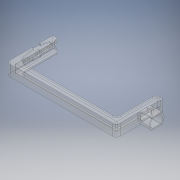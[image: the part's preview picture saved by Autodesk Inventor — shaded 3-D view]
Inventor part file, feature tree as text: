
AUTODESK INVENTOR PART (.ipt)
format: ipt  version: 2018 (Build 220112000, 112)  size: 311,808 bytes
history: native  units: mm
features: extrude x7, sketch x7, fillet x4, chamfer x4
ambient origin geometry x8: Origin, YZ Plane, XZ Plane, XY Plane, X Axis, Y Axis, Z Axis, Center Point
bodies: Solid1 (feature_tree)
feature tree (22):
  extrude  "Phone Profile"  Depth=72.5mm
  extrude  "Front Wall"  Depth=5.0mm
  extrude  "Back Wall"  Depth=155.0mm
  fillet  "Strengthening fillet"  Radius=65.3125mm
  extrude  "Servo Holes"  Depth=11.5mm TaperAngle=0.0deg
  extrude  "Servo indentation"  Depth=5.0mm
  chamfer  "Servo Chamfer 1"  Distance=2.0mm
  chamfer  "Servo Chamfer 2"  Distance=2.0mm
  extrude  "Charge Port"  Depth=2.0mm
  fillet  "Fillet Profile"  Radius=23.8125mm
  extrude  "Mount"  Depth=2.0mm
  fillet  "Charge Fillet"  Radius=6.5mm
  chamfer  "Upper Servo Chamfer 1"  Distance=1.5mm
  chamfer  "Upper Servo Chamfer 2"  Distance=39.5mm
  fillet  "Servo Fillets"  Radius=20.0mm
  sketch  "Sketch1"  dims[d0=72.5mm d1=72.5mm]
  sketch  "Sketch2"  dims[d2=60.3125mm d3=5.0mm]
  sketch  "Sketch3"  dims[d4=65.3125mm d5=155.0mm d6=65.3125mm]
  sketch  "Sketch4"  dims[d7=5.0mm d8=11.5mm d9=0.0mm]
  sketch  "Sketch5"  dims[d10=5.0mm d11=5.0mm]
  sketch  "Sketch6"  dims[d12=55.3125mm]
  sketch  "Sketch7"  dims[d13=55.3125mm d14=2.0mm d15=0.0mm d16=2.0mm d17=0.0mm d18=2.0mm d20=23.8125mm d21=14.0mm d22=6.5mm d23=1.5mm d24=39.5mm d25=0.0mm d26=20.0mm d27=10.0mm d28=5.0mm d29=5.0mm d30=2.0mm d31=0.0mm d32=10.0mm d33=2.0mm d34=15.0deg d35=10.0mm d36=2.0mm d37=15.0deg d38=15.0mm d39=6.5mm d40=0.0mm d41=5.0mm d42=20.0mm d43=14.0mm d44=1.5mm d47=21.0mm d48=15.0mm d49=0.0mm d50=2.0mm d51=10.0mm d52=2.0mm d53=15.0deg d54=10.0mm d55=2.0mm d56=15.0deg d57=2.0mm]
